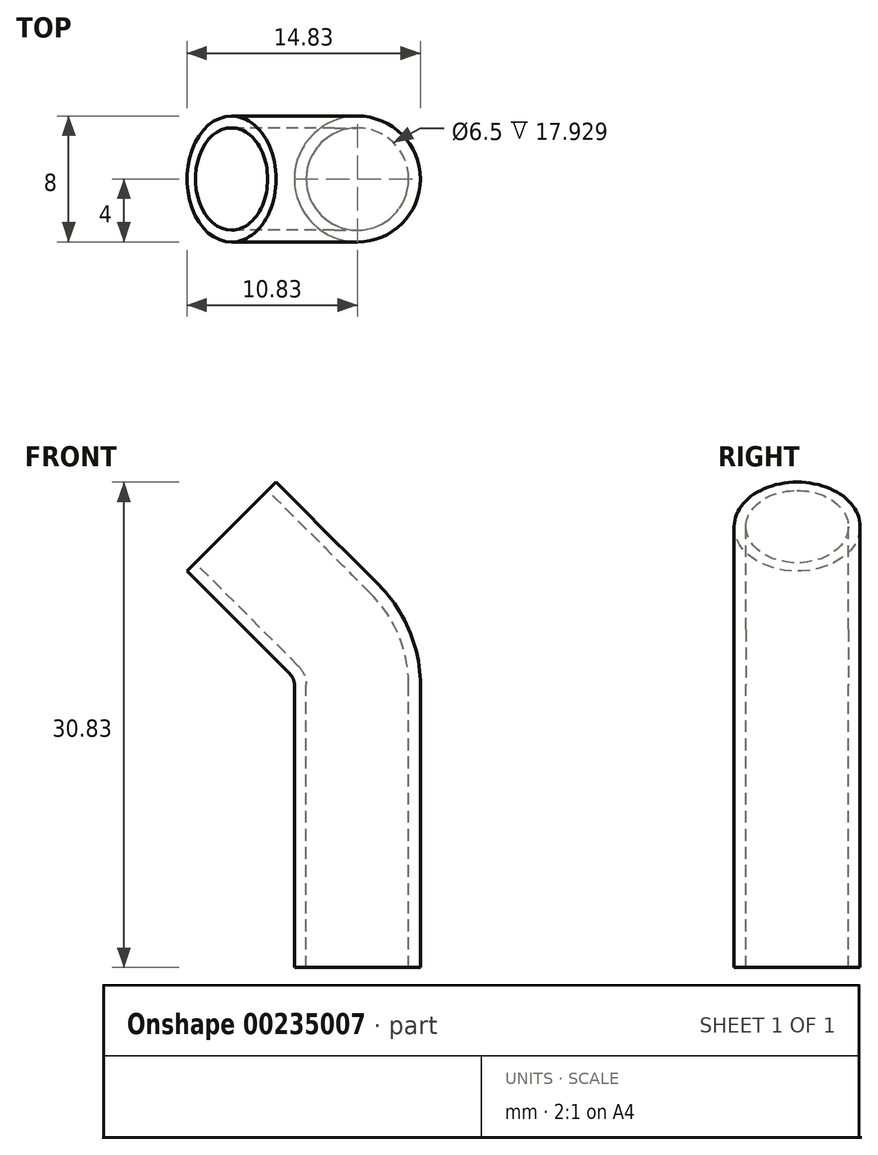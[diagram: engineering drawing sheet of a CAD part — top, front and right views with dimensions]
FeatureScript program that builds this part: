
annotation { "Feature Type Name" : "Feature", "Feature Type Description" : "" }
export const myFeature = defineFeature(function(context is Context, id is Id, definition is map)
    precondition{}
    {
        {
            var Q0;
            Q0=qCreatedBy(makeId("Front.planeOp"),FACE);
            var sketch = newSketch(context, id + "F0", { "sketchPlane" : qUnion([Q0])});
            skLineSegment(sketch, "E0", {"start": v(0, 0) * mm, "end": v(0, 17.93) * mm});
            skLineSegment(sketch, "E1", {"start": v(-1.46, 21.46) * mm, "end": v(-8, 28) * mm});
            skPoint(sketch, "E2.visualSharp", {"position": v(0, 20) * mm});
            skArc(sketch, "E2.filletArc", {"start": v(0, 17.93) * mm, "mid": v(-0.38, 19.84) * mm, "end": v(-1.46, 21.46) * mm});
            skSolve(sketch);
        }
        {
            var Q0;
            Q0=qCreatedBy(makeId("Top.planeOp"),FACE);
            var sketch = newSketch(context, id + "F1", { "sketchPlane" : qUnion([Q0])});
            skCircle(sketch, "E3", {"center": v(0, 0) * mm, "radius": 3.25 * mm});
            skCircle(sketch, "E4", {"center": v(0, 0) * mm, "radius": 4 * mm});
            skSolve(sketch);
        }
        {
            var Q0;
            Q0 = qSketchRegion(id + "F1", true);
            var Q1;
            Q1 = qConstructionFilter(qBodyType(qCreatedBy(id + "F1" ,EDGE), BodyType.WIRE), ConstructionObject.NO);
            var Q2;
            Q2=sQuery(id+"F0.wireOp",EDGE,"E0");
            var Q3;
            Q3=sQuery(id+"F0.wireOp",EDGE,"E2.filletArc");
            var Q4;
            Q4=sQuery(id+"F0.wireOp",EDGE,"E1");
            sweep(context, id + "F2", {"profiles" : qUnion([Q0]), "surfaceProfiles" : qUnion([Q1]), "path" : qUnion([Q2, Q3, Q4])});
        }
    });
